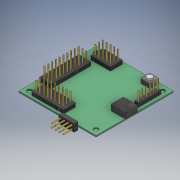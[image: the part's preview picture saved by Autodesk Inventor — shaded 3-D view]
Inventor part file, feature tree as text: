
AUTODESK INVENTOR PART (.ipt)
format: ipt  version: 2017 (Build 210142000, 142)  size: 545,280 bytes
history: native  units: mm
features: extrude x11, sketch x8, pattern_linear x5, projected_geometry x4, other x1
ambient origin geometry x8: Origin, YZ Plane, XZ Plane, XY Plane, X Axis, Y Axis, Z Axis, Center Point
bodies: Body1 (feature_tree)
feature tree (29):
  other  "Bryła1"
  extrude  "Wyciągnięcie proste1"  Depth=51.0mm
  extrude  "Wyciągnięcie proste2"  Depth=51.0mm
  sketch  "Szkic3"
  extrude  "Wyciągnięcie proste3"  Depth=3.0mm
  pattern_linear  "Szyk prostokątny1"  Spacing1=3.5mm  [1 undecoded]
  extrude  "Wyciągnięcie proste4"  Depth=3.5mm
  pattern_linear  "Szyk prostokątny2"  Count1=4 Spacing1=360.0deg
  extrude  "Wyciągnięcie proste5"  Depth=1.0mm TaperAngle=0.0deg
  pattern_linear  "Szyk prostokątny3"  Spacing1=8.0mm  [1 undecoded]
  extrude  "Wyciągnięcie proste6"  Depth=13.0mm
  pattern_linear  "Szyk prostokątny4"  Spacing1=6.0mm  [1 undecoded]
  extrude  "Wyciągnięcie proste7"  Depth=1.5mm
  extrude  "Wyciągnięcie proste8"  Depth=26.0mm
  extrude  "Wyciągnięcie proste9"  Depth=8.0mm
  extrude  "Wyciągnięcie proste10"  Depth=13.0mm
  extrude  "Wyciągnięcie proste11"  Depth=1.5mm
  pattern_linear  "Szyk prostokątny5"  Spacing1=8.0mm  [1 undecoded]
  sketch  "Szkic1"
  sketch  "Szkic2"
  projected_geometry  "Pętla rzutowana1"
  projected_geometry  "Pętla rzutowana2"
  projected_geometry  "Pętla rzutowana3"
  projected_geometry  "Pętla rzutowana4"
  sketch  "Szkic4"
  sketch  "Szkic5"
  sketch  "Szkic6"
  sketch  "Szkic7"
  sketch  "Szkic8"
note: 4 required parameter values undecoded (feature->parameter linkage not recoverable at this tier; creation-order binding heuristic only, values carry confidence <= 0.55)
